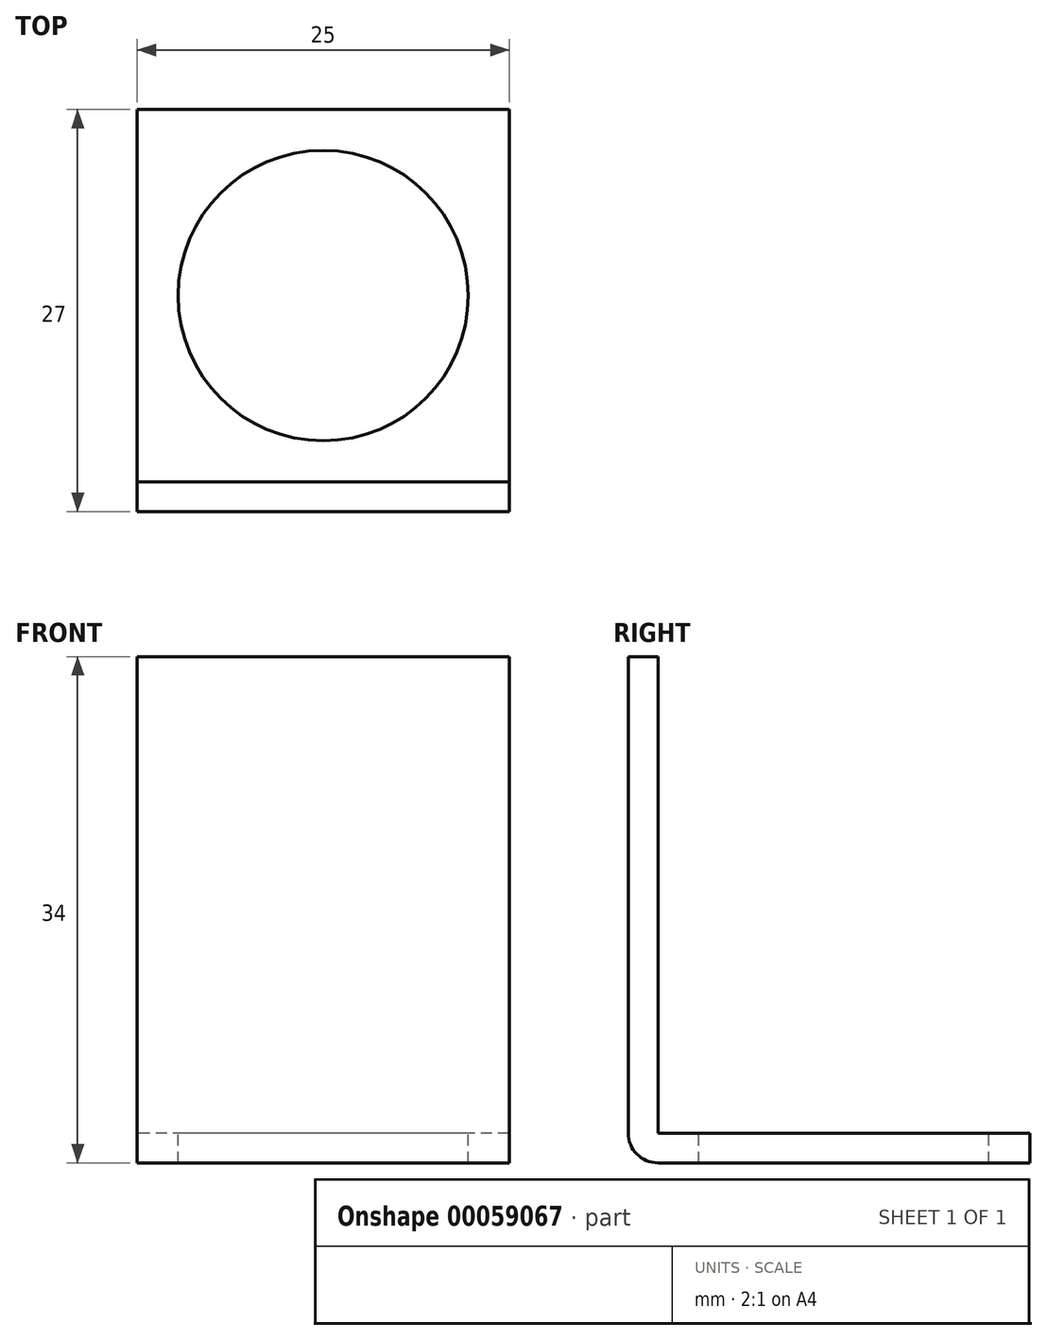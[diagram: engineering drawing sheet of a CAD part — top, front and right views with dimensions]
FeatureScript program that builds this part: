
annotation { "Feature Type Name" : "Feature", "Feature Type Description" : "" }
export const myFeature = defineFeature(function(context is Context, id is Id, definition is map)
    precondition{}
    {
        {
            var Q0;
            Q0=qCreatedBy(makeId("Front.planeOp"),FACE);
            var sketch = newSketch(context, id + "F0", { "sketchPlane" : qUnion([Q0])});
            skLineSegment(sketch, "E0.bottom", {"start": v(-12.5, 0) * mm, "end": v(12.5, 0) * mm});
            skLineSegment(sketch, "E0.top", {"start": v(-12.5, 34) * mm, "end": v(12.5, 34) * mm});
            skLineSegment(sketch, "E0.left", {"start": v(-12.5, 0) * mm, "end": v(-12.5, 34) * mm});
            skLineSegment(sketch, "E0.right", {"start": v(12.5, 0) * mm, "end": v(12.5, 34) * mm});
            skSolve(sketch);
        }
        {
            var Q0;
            Q0=makeQuery(id+"F0.imprint","IMPRINT",FACE,{"disambiguationData":[TD([[makeQuery(id+"F0.imprint","IMPRINT",EDGE,{"derivedFrom":sQuery(id+"F0.wireOp",EDGE,"E0.bottom")}),1.0]])]});
            extrude(context, id + "F1", {"entities" : qUnion([Q0]), "depth" : 2 * mm});
        }
        {
            var Q0;
            Q0=qCreatedBy(makeId("Top.planeOp"),FACE);
            var sketch = newSketch(context, id + "F2", { "sketchPlane" : qUnion([Q0])});
            skLineSegment(sketch, "E1.bottom", {"start": v(12.5, 0) * mm, "end": v(-12.5, 0) * mm});
            skLineSegment(sketch, "E1.top", {"start": v(12.5, 25) * mm, "end": v(-12.5, 25) * mm});
            skLineSegment(sketch, "E1.left", {"start": v(12.5, 0) * mm, "end": v(12.5, 25) * mm});
            skLineSegment(sketch, "E1.right", {"start": v(-12.5, 0) * mm, "end": v(-12.5, 25) * mm});
            skSolve(sketch);
        }
        {
            var Q0;
            Q0=makeQuery(id+"F2.imprint","IMPRINT",FACE,{"disambiguationData":[TD([[makeQuery(id+"F2.imprint","IMPRINT",EDGE,{"derivedFrom":sQuery(id+"F2.wireOp",EDGE,"E1.bottom")}),-1.0]])]});
            extrude(context, id + "F3", {"entities" : qUnion([Q0]), "operationType" : NewBodyOperationType.ADD, "depth" : 2 * mm});
        }
        {
            var Q0;
            Q0=makeQuery(id+"F3.opExtrude","CAP_FACE",FACE,{"disambiguationData":[OSD([sQuery(id+"F2.wireOp",EDGE,"E1.bottom"),sQuery(id+"F2.wireOp",EDGE,"E1.top"),sQuery(id+"F2.wireOp",EDGE,"E1.left"),sQuery(id+"F2.wireOp",EDGE,"E1.right")])],"isStart":false});
            var sketch = newSketch(context, id + "F4", { "sketchPlane" : qUnion([Q0])});
            skCircle(sketch, "E2", {"center": v(0, 12.5) * mm, "radius": 9.75 * mm});
            skLineSegment(sketch, "E3", {"start": v(0, 0) * mm, "end": v(0, 25) * mm, "construction": true});
            skSolve(sketch);
        }
        {
            var Q0;
            Q0=makeQuery(id+"F4.imprint","IMPRINT",FACE,{"disambiguationData":[TD([[makeQuery(id+"F4.imprint","IMPRINT",EDGE,{"derivedFrom":sQuery(id+"F4.wireOp",EDGE,"E2")}),1.0]])]});
            extrude(context, id + "F5", {"entities" : qUnion([Q0]), "operationType" : NewBodyOperationType.REMOVE, "endBound" : BoundingType.THROUGH_ALL, "oppositeDirection" : true, "depth" : 25.4 * mm});
        }
        {
            var Q0;
            Q0=makeQuery(id+"F1.opExtrude","CAP_EDGE",EDGE,{"disambiguationData":[OSD([sQuery(id+"F0.wireOp",EDGE,"E0.bottom")])],"isStart":false});
            var Q1;
            Q1=makeQuery(id+"F3.opExtrude","CAP_EDGE",EDGE,{"disambiguationData":[OSD([sQuery(id+"F2.wireOp",EDGE,"E1.bottom")])],"isStart":false});
            fillet(context, id + "F6", {"entities" : qUnion([Q0, Q1]), "radius" : 2 * mm, "tangentPropagation" : true, "allowEdgeOverflow" : false});
        }
    });
